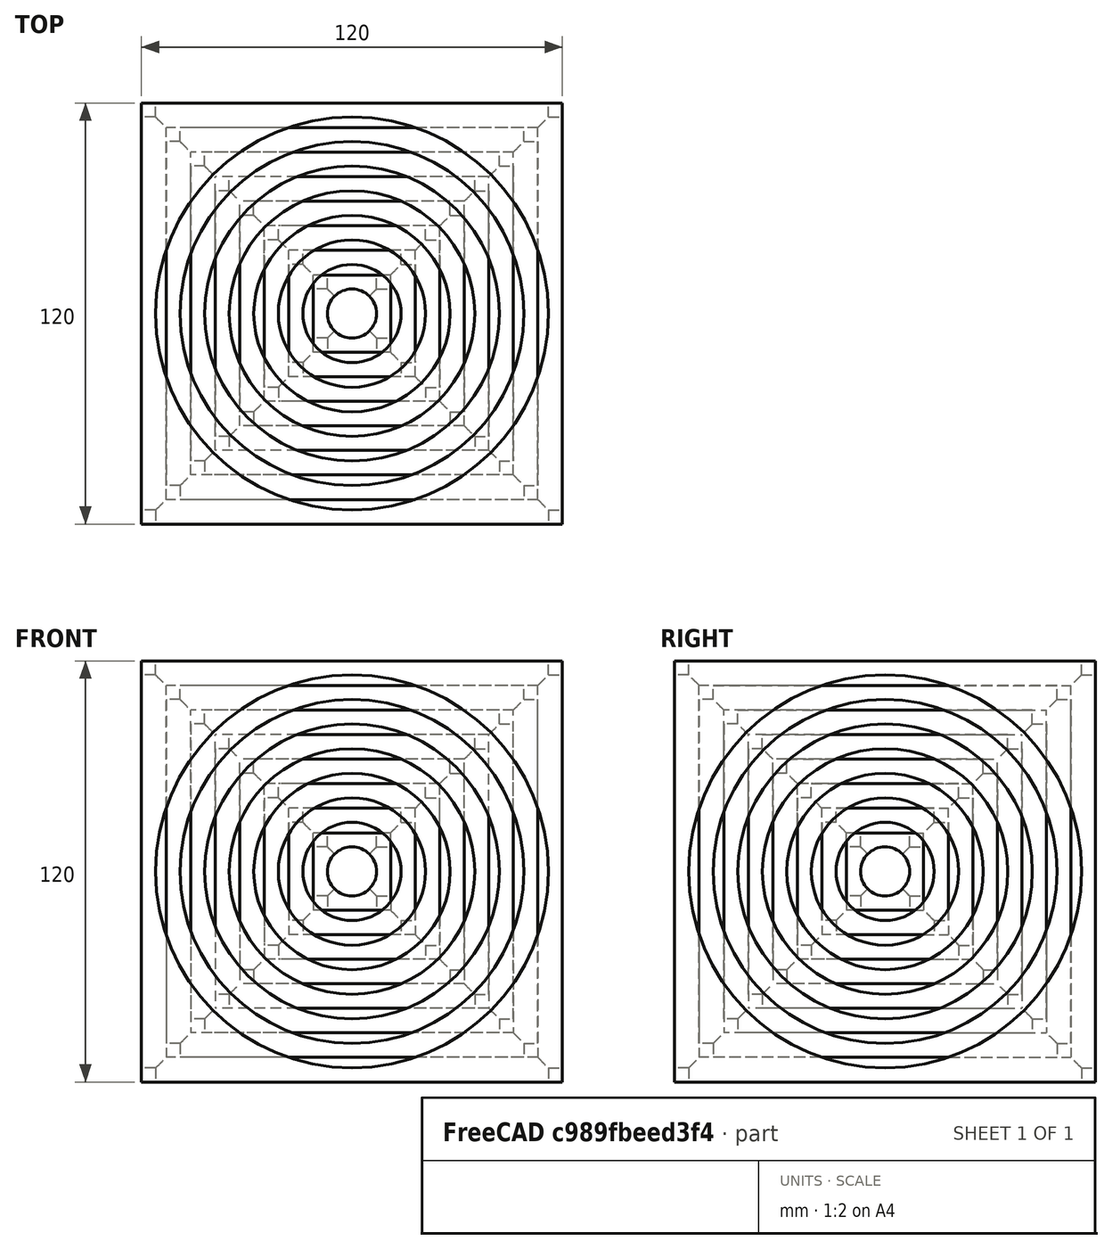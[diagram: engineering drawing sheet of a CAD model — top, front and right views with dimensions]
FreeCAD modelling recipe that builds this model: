
FCSTD DOCUMENT  (FreeCAD 0.20R29603 (Git))
Label: f2b_wuerfel
License: All rights reserved
LicenseURL: http://en.wikipedia.org/wiki/All_rights_reserved
objects: Sketcher::SketchObject×2, PartDesign::PolarPattern×2, PartDesign::Pad×1, PartDesign::Groove×1, PartDesign::Body×1, Mesh::Feature×1
note: 9 computed .brp shape members not serialized (recipe doc carries the construction recipe); baked Part::Feature solids carry a one-line shape summary decoded from their .brp

FEATURE [Sketcher::SketchObject] Sketch  label="sk_wuerfel"
  FullyConstrained = true
  MapMode = 5
  Support = -> [XY_Plane]
  sketch-geometry (5):
    g0: LineSegment StartX=-60 StartY=60 StartZ=0 EndX=-60 EndY=-60 EndZ=0
    g1: LineSegment StartX=-60 StartY=-60 StartZ=0 EndX=60 EndY=-60 EndZ=0
    g2: LineSegment StartX=60 StartY=-60 StartZ=0 EndX=60 EndY=60 EndZ=0
    g3: LineSegment StartX=60 StartY=60 StartZ=0 EndX=-60 EndY=60 EndZ=0
    g4: GeomPoint X=0 Y=0 Z=0
  constraints (12):
    c: Coincident(g0,g1)
    c: Coincident(g1,g2)
    c: Coincident(g2,g3)
    c: Coincident(g3,g0)
    c: Horizontal(g1)
    c: Horizontal(g3)
    c: Vertical(g0)
    c: Vertical(g2)
    c: Symmetric(g1,g0,g4)
    c: Coincident(g4,g-1)
    c: Equal(g3,g2)
    c: DistanceX(g3,g3) = 120  'd_kante'
FEATURE [PartDesign::Pad] Pad  label="pad_wuerfel"
  Direction = (0,0,1)
  Length = 120
  Length2 = 10
  Midplane = true
  Profile = -> Sketch
  ReferenceAxis = -> Sketch [N_Axis]
  Type = 0
  expr: Length = <<sk_wuerfel>>.Constraints.d_kante
FEATURE [Sketcher::SketchObject] Sketch001  label="sk_freimachung"
  FullyConstrained = true
  MapMode = 5
  Placement = pos=(0,0,0) rot=(1,0,0;1.5708rad)
  Support = -> [XZ_Plane]
  expr: Constraints[4] = <<sk_wuerfel>>.Constraints.d_kante / 2
  sketch-geometry (18):
    g0: LineSegment StartX=0 StartY=60 StartZ=0 EndX=0 EndY=4 EndZ=0
    g1: LineSegment StartX=56 StartY=60 StartZ=0 EndX=0 EndY=60 EndZ=0
    g2: LineSegment StartX=0 StartY=4 StartZ=0 EndX=7 EndY=4 EndZ=0
    g3: LineSegment StartX=7 StartY=4 StartZ=0 EndX=7 EndY=11 EndZ=0
    g4: LineSegment StartX=7 StartY=11 StartZ=0 EndX=14 EndY=11 EndZ=0
    g5: LineSegment StartX=14 StartY=11 StartZ=0 EndX=14 EndY=18 EndZ=0
    g6: LineSegment StartX=14 StartY=18 StartZ=0 EndX=21 EndY=18 EndZ=0
    g7: LineSegment StartX=21 StartY=18 StartZ=0 EndX=21 EndY=25 EndZ=0
    g8: LineSegment StartX=21 StartY=25 StartZ=0 EndX=28 EndY=25 EndZ=0
    g9: LineSegment StartX=28 StartY=25 StartZ=0 EndX=28 EndY=32 EndZ=0
    g10: LineSegment StartX=28 StartY=32 StartZ=0 EndX=35 EndY=32 EndZ=0
    g11: LineSegment StartX=35 StartY=32 StartZ=0 EndX=35 EndY=39 EndZ=0
    g12: LineSegment StartX=35 StartY=39 StartZ=0 EndX=42 EndY=39 EndZ=0
    g13: LineSegment StartX=42 StartY=39 StartZ=0 EndX=42 EndY=46 EndZ=0
    g14: LineSegment StartX=42 StartY=46 StartZ=0 EndX=49 EndY=46 EndZ=0
    g15: LineSegment StartX=49 StartY=46 StartZ=0 EndX=49 EndY=53 EndZ=0
    g16: LineSegment StartX=49 StartY=53 StartZ=0 EndX=56 EndY=53 EndZ=0
    g17: LineSegment StartX=56 StartY=53 StartZ=0 EndX=56 EndY=60 EndZ=0
  constraints (55):
    c: Vertical(g0)
    c: Horizontal(g1)
    c: Coincident(g0,g1)
    c: PointOnObject(g0,g-2)
    c: DistanceY(g-1,g0) = 60
    c: Equal(g1,g0)
    c: Coincident(g0,g2)
    c: Horizontal(g2)
    c: Coincident(g2,g3)
    c: Vertical(g3)
    c: Coincident(g3,g4)
    c: Horizontal(g4)
    c: Coincident(g4,g5)
    c: Coincident(g5,g6)
    c: Coincident(g6,g7)
    c: Coincident(g7,g8)
    c: Coincident(g8,g9)
    c: Coincident(g9,g10)
    c: Coincident(g10,g11)
    c: Vertical(g11)
    c: Coincident(g11,g12)
    c: Horizontal(g12)
    c: Coincident(g12,g13)
    c: Vertical(g13)
    c: Coincident(g13,g14)
    c: Horizontal(g14)
    c: Coincident(g14,g15)
    c: Vertical(g15)
    c: Coincident(g15,g16)
    c: Horizontal(g16)
    c: Coincident(g16,g17)
    c: Coincident(g17,g1)
    c: Vertical(g17)
    c: Vertical(g9)
    c: Vertical(g7)
    c: Vertical(g5)
    c: Horizontal(g10)
    c: Horizontal(g6)
    c: Horizontal(g8)
    c: Equal(g2,g4)
    c: Equal(g4,g6)
    c: Equal(g8,g10)
    c: Equal(g10,g12)
    c: Equal(g12,g14)
    c: Equal(g14,g16)
    c: Equal(g3,g5)
    c: Equal(g5,g7)
    c: Equal(g7,g9)
    c: Equal(g9,g11)
    c: Equal(g11,g13)
    c: Equal(g13,g15)
    c: Equal(g15,g17)
    c: Equal(g6,g8)
    c: DistanceY(g0,g0) = 56
    c: DistanceX(g2,g2) = 7  'd_tiefe'
FEATURE [PartDesign::Groove] Groove  label="nut_freimachung"
  Angle = 360
  Axis = (-3e-16,3e-16,1)
  Base = (0,0,0)
  BaseFeature = -> Pad
  Profile = -> Sketch001
  ReferenceAxis = -> Z_Axis
FEATURE [PartDesign::PolarPattern] PolarPattern  label="PolarPattern_X"
  Angle = 360
  Axis = -> X_Axis
  BaseFeature = -> Groove
  Occurrences = 4
  Originals = -> [Groove]
FEATURE [PartDesign::PolarPattern] PolarPattern001  label="PolarPattern_Y"
  Angle = 360
  Axis = -> Y_Axis
  BaseFeature = -> PolarPattern
  Occurrences = 4
  Originals = -> [Groove]
FEATURE [PartDesign::Body] Body
  Group = -> [Sketch,Pad,Sketch001,Groove,PolarPattern,PolarPattern001]
  Origin = -> Origin
  Tip = -> PolarPattern001
FEATURE [Mesh::Feature] Mesh  label="PolarPattern_Y (Meshed)"
